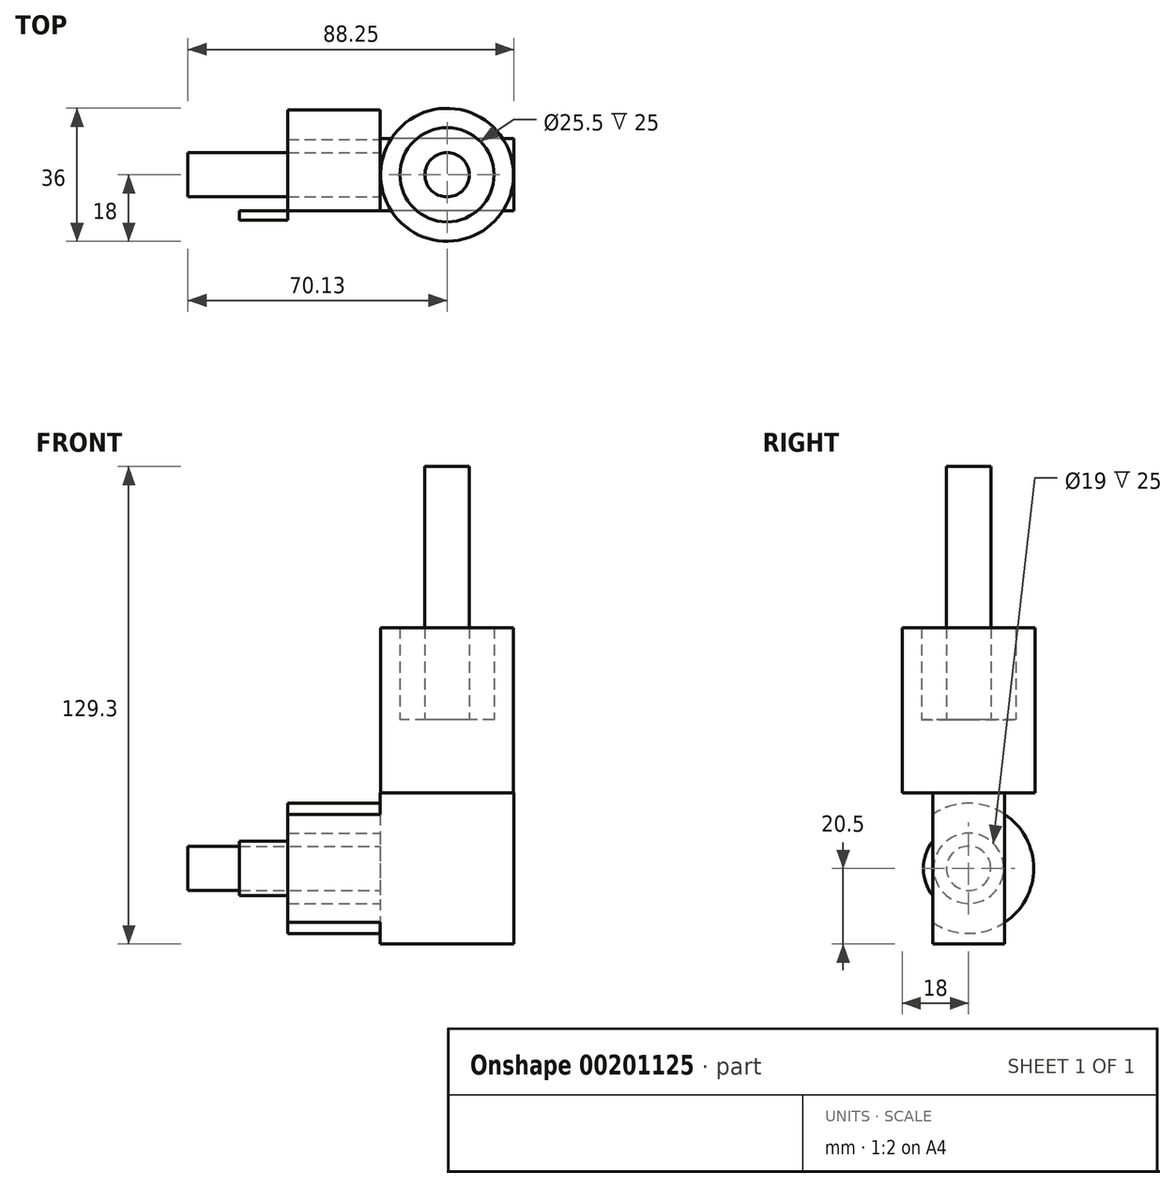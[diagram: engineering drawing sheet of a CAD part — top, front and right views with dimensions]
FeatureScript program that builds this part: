
annotation { "Feature Type Name" : "Feature", "Feature Type Description" : "" }
export const myFeature = defineFeature(function(context is Context, id is Id, definition is map)
    precondition{}
    {
        {
            var Q0;
            Q0=qCreatedBy(makeId("Right.planeOp"),FACE);
            var sketch = newSketch(context, id + "F0", { "sketchPlane" : qUnion([Q0])});
            skLineSegment(sketch, "E0.bottom", {"start": v(-9.75, 20.5) * mm, "end": v(9.75, 20.5) * mm});
            skLineSegment(sketch, "E0.top", {"start": v(-9.75, -20.5) * mm, "end": v(9.75, -20.5) * mm});
            skLineSegment(sketch, "E0.left", {"start": v(-9.75, 20.5) * mm, "end": v(-9.75, -20.5) * mm});
            skLineSegment(sketch, "E0.right", {"start": v(9.75, 20.5) * mm, "end": v(9.75, -20.5) * mm});
            skPoint(sketch, "E0.middle", {"position": v(0, 0) * mm});
            skSolve(sketch);
        }
        {
            var Q0;
            Q0=makeQuery(id+"F0.imprint","IMPRINT",FACE,{"disambiguationData":[TD([[makeQuery(id+"F0.imprint","IMPRINT",EDGE,{"derivedFrom":sQuery(id+"F0.wireOp",EDGE,"E0.bottom")}),-1.0]])]});
            extrude(context, id + "F1", {"entities" : qUnion([Q0]), "endBound" : BoundingType.SYMMETRIC, "depth" : 36.25 * mm, "offsetDistance" : 25 * mm});
        }
        {
            var Q0;
            Q0=makeQuery(id+"F1.opExtrude","SWEPT_FACE",FACE,{"disambiguationData":[OSD([sQuery(id+"F0.wireOp",EDGE,"E0.bottom")])]});
            var sketch = newSketch(context, id + "F2", { "sketchPlane" : qUnion([Q0])});
            skCircle(sketch, "E1", {"center": v(0, 0) * mm, "radius": 18 * mm});
            skSolve(sketch);
        }
        {
            var Q0;
            Q0 = qSketchRegion(id + "F2", true);
            extrude(context, id + "F3", {"entities" : qUnion([Q0]), "operationType" : NewBodyOperationType.ADD, "depth" : 19.7 * mm, "offsetDistance" : 25 * mm});
        }
        {
            var Q0;
            Q0=makeQuery(id+"F3.opExtrude","CAP_FACE",FACE,{"disambiguationData":[OSD([sQuery(id+"F2.wireOp",EDGE,"E1")])],"isStart":false});
            var sketch = newSketch(context, id + "F4", { "sketchPlane" : qUnion([Q0])});
            skCircle(sketch, "E2", {"center": v(0, 0) * mm, "radius": 12.75 * mm});
            skCircle(sketch, "E3", {"center": v(0, 0) * mm, "radius": 6 * mm});
            skSolve(sketch);
        }
        {
            var Q0;
            Q0=makeQuery(id+"F4.imprint","IMPRINT",FACE,{"disambiguationData":[TD([[makeQuery(id+"F4.imprint","IMPRINT",EDGE,{"derivedFrom":sQuery(id+"F4.wireOp",EDGE,"E2")}),-1.0]])]});
            extrude(context, id + "F5", {"entities" : qUnion([Q0]), "operationType" : NewBodyOperationType.ADD, "depth" : 25 * mm, "offsetDistance" : 25 * mm});
        }
        {
            var Q0;
            Q0=makeQuery(id+"F4.imprint","IMPRINT",FACE,{"disambiguationData":[TD([[makeQuery(id+"F4.imprint","IMPRINT",EDGE,{"derivedFrom":sQuery(id+"F4.wireOp",EDGE,"E3")}),1.0]])]});
            extrude(context, id + "F6", {"entities" : qUnion([Q0]), "depth" : 68.6 * mm, "offsetDistance" : 25 * mm});
        }
        {
            var Q0;
            Q0=makeQuery(id+"F1.opExtrude","CAP_FACE",FACE,{"disambiguationData":[OSD([sQuery(id+"F0.wireOp",EDGE,"E0.bottom"),sQuery(id+"F0.wireOp",EDGE,"E0.top"),sQuery(id+"F0.wireOp",EDGE,"E0.left"),sQuery(id+"F0.wireOp",EDGE,"E0.right")])],"isStart":true});
            var sketch = newSketch(context, id + "F7", { "sketchPlane" : qUnion([Q0])});
            skCircle(sketch, "E4", {"center": v(0, 0) * mm, "radius": 17.6 * mm});
            skCircle(sketch, "E5", {"center": v(0, 0) * mm, "radius": 6 * mm});
            skCircle(sketch, "E6", {"center": v(0, 0) * mm, "radius": 9.5 * mm});
            skSolve(sketch);
        }
        {
            var Q0;
            {var subQ0=sQuery(id+"F7.wireOp",EDGE,"E4");var subQ1=makeQuery(id+"F1.opExtrude","CAP_EDGE",EDGE,{"disambiguationData":[OSD([sQuery(id+"F0.wireOp",EDGE,"E0.right")])],"isStart":true});var subQ2=makeQuery(id+"F7.imprint","INTERSECT",VERTEX,{"disambiguationData":[OD(1.0)],"derivedFrom":[subQ1,subQ0]});Q0=makeQuery(id+"F7.imprint","IMPRINT",FACE,{"disambiguationData":[TD([[makeQuery(id+"F7.imprint","IMPRINT",EDGE,{"disambiguationData":[TD([[subQ2,-1.0]])],"derivedFrom":subQ0}),1.0]])]});}
            var Q1;
            {var subQ0=sQuery(id+"F7.wireOp",EDGE,"E4");var subQ1=makeQuery(id+"F1.opExtrude","CAP_EDGE",EDGE,{"disambiguationData":[OSD([sQuery(id+"F0.wireOp",EDGE,"E0.right")])],"isStart":true});var subQ2=makeQuery(id+"F7.imprint","INTERSECT",VERTEX,{"disambiguationData":[OD(0.0)],"derivedFrom":[subQ1,subQ0]});Q1=makeQuery(id+"F7.imprint","IMPRINT",FACE,{"disambiguationData":[TD([[makeQuery(id+"F7.imprint","IMPRINT",EDGE,{"disambiguationData":[TD([[subQ2,1.0]])],"derivedFrom":subQ0}),1.0]])]});}
            var Q2;
            {var subQ0=sQuery(id+"F7.wireOp",EDGE,"E4");var subQ1=makeQuery(id+"F1.opExtrude","CAP_EDGE",EDGE,{"disambiguationData":[OSD([sQuery(id+"F0.wireOp",EDGE,"E0.left")])],"isStart":true});var subQ2=makeQuery(id+"F7.imprint","INTERSECT",VERTEX,{"disambiguationData":[OD(0.0)],"derivedFrom":[subQ1,subQ0]});Q2=makeQuery(id+"F7.imprint","IMPRINT",FACE,{"disambiguationData":[TD([[makeQuery(id+"F7.imprint","IMPRINT",EDGE,{"disambiguationData":[TD([[subQ2,1.0]])],"derivedFrom":subQ0}),1.0]])]});}
            var Q3;
            {var subQ0=sQuery(id+"F7.wireOp",EDGE,"E4");var subQ1=makeQuery(id+"F1.opExtrude","CAP_EDGE",EDGE,{"disambiguationData":[OSD([sQuery(id+"F0.wireOp",EDGE,"E0.right")])],"isStart":true});var subQ2=makeQuery(id+"F7.imprint","INTERSECT",VERTEX,{"disambiguationData":[OD(0.0)],"derivedFrom":[subQ1,subQ0]});Q3=makeQuery(id+"F7.imprint","IMPRINT",FACE,{"disambiguationData":[TD([[makeQuery(id+"F7.imprint","IMPRINT",EDGE,{"disambiguationData":[TD([[subQ2,-1.0]])],"derivedFrom":subQ0}),1.0]])]});}
            extrude(context, id + "F8", {"entities" : qUnion([Q0, Q1, Q2, Q3]), "operationType" : NewBodyOperationType.ADD, "depth" : 25 * mm, "offsetDistance" : 25 * mm});
        }
        {
            var Q0;
            Q0=makeQuery(id+"F8.opExtrude","CAP_FACE",FACE,{"disambiguationData":[OSD([sQuery(id+"F7.wireOp",EDGE,"E4"),sQuery(id+"F7.wireOp",EDGE,"E6")])],"isStart":false});
            var sketch = newSketch(context, id + "F9", { "sketchPlane" : qUnion([Q0])});
            skCircle(sketch, "E7", {"center": v(0, 0) * mm, "radius": 12.25 * mm});
            skSolve(sketch);
        }
        {
            var Q0;
            Q0=makeQuery(id+"F9.imprint","IMPRINT",FACE,{"disambiguationData":[TD([[makeQuery(id+"F9.imprint","IMPRINT",EDGE,{"derivedFrom":sQuery(id+"F9.wireOp",EDGE,"E7")}),1.0]])]});
            extrude(context, id + "F10", {"entities" : qUnion([Q0]), "operationType" : NewBodyOperationType.ADD, "depth" : 13.14 * mm, "offsetDistance" : 25 * mm});
        }
        {
            var Q0;
            Q0=makeQuery(id+"F7.imprint","IMPRINT",FACE,{"disambiguationData":[TD([[makeQuery(id+"F7.imprint","IMPRINT",EDGE,{"derivedFrom":sQuery(id+"F7.wireOp",EDGE,"E5")}),1.0]])]});
            extrude(context, id + "F11", {"entities" : qUnion([Q0]), "depth" : 52 * mm, "offsetDistance" : 25 * mm});
        }
    });
